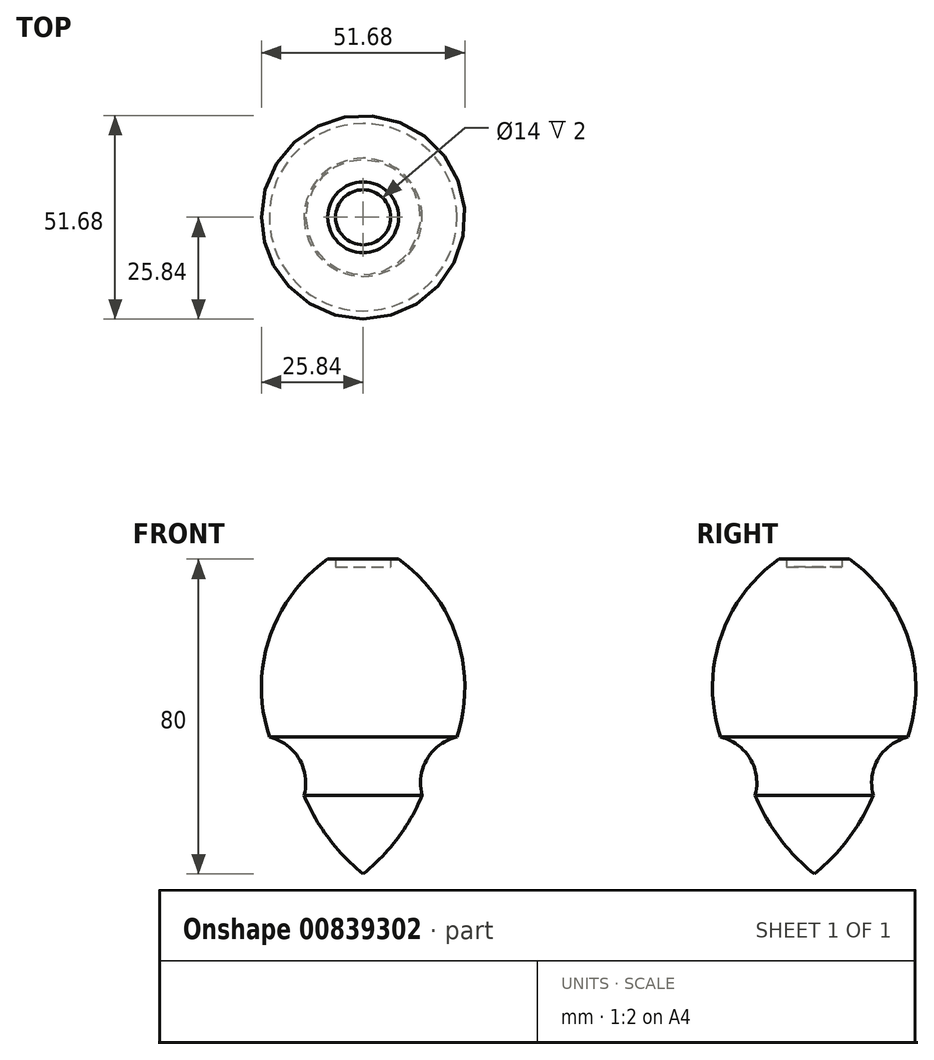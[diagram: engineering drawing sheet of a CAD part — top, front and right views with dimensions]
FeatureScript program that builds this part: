
annotation { "Feature Type Name" : "Feature", "Feature Type Description" : "" }
export const myFeature = defineFeature(function(context is Context, id is Id, definition is map)
    precondition{}
    {
        {
            var Q0;
            Q0=qCreatedBy(makeId("Front.planeOp"),FACE);
            var sketch = newSketch(context, id + "F0", { "sketchPlane" : qUnion([Q0])});
            skLineSegment(sketch, "E0", {"start": v(0, 0) * mm, "end": v(0, 80) * mm});
            skLineSegment(sketch, "E1", {"start": v(0, 80) * mm, "end": v(9, 80) * mm});
            skLineSegment(sketch, "E2", {"start": v(0, 20) * mm, "end": v(15, 20) * mm});
            skLineSegment(sketch, "E3", {"start": v(0, 40) * mm, "end": v(0, 0) * mm});
            skArc(sketch, "E4", {"start": v(23.81, 34.8) * mm, "mid": v(23.85, 59.84) * mm, "end": v(9, 80) * mm});
            skLineSegment(sketch, "E5", {"start": v(23.81, 34.8) * mm, "end": v(0, 34.8) * mm});
            skArc(sketch, "E6", {"start": v(23.81, 34.8) * mm, "mid": v(16.27, 29.27) * mm, "end": v(15, 20) * mm});
            skArc(sketch, "E7", {"start": v(0, 0) * mm, "mid": v(8.77, 9.05) * mm, "end": v(15, 20) * mm});
            skLineSegment(sketch, "E8", {"start": v(7, 78) * mm, "end": v(0, 78) * mm});
            skLineSegment(sketch, "E9", {"start": v(7, 78) * mm, "end": v(7, 80) * mm});
            skSolve(sketch);
        }
        {
            var Q0;
            {var subQ0=sQuery(id+"F0.wireOp",EDGE,"E4");Q0=makeQuery(id+"F0.imprint","IMPRINT",FACE,{"disambiguationData":[TD([[makeQuery(id+"F0.imprint","IMPRINT",EDGE,{"derivedFrom":subQ0}),1.0]])]});}
            var Q1;
            {var subQ0=sQuery(id+"F0.wireOp",EDGE,"E2");Q1=makeQuery(id+"F0.imprint","IMPRINT",FACE,{"disambiguationData":[TD([[makeQuery(id+"F0.imprint","IMPRINT",EDGE,{"derivedFrom":subQ0}),1.0]])]});}
            var Q2;
            {var subQ0=sQuery(id+"F0.wireOp",EDGE,"E2");Q2=makeQuery(id+"F0.imprint","IMPRINT",FACE,{"disambiguationData":[TD([[makeQuery(id+"F0.imprint","IMPRINT",EDGE,{"derivedFrom":subQ0}),-1.0]])]});}
            var Q3;
            Q3=sQuery(id+"F0.wireOp",EDGE,"E0");
            revolve(context, id + "F1", {"surfaceOperationType" : NewSurfaceOperationType.NEW, "entities" : qUnion([Q0, Q1, Q2]), "axis" : qUnion([Q3]), "revolveType" : RevolveType.FULL});
        }
    });
